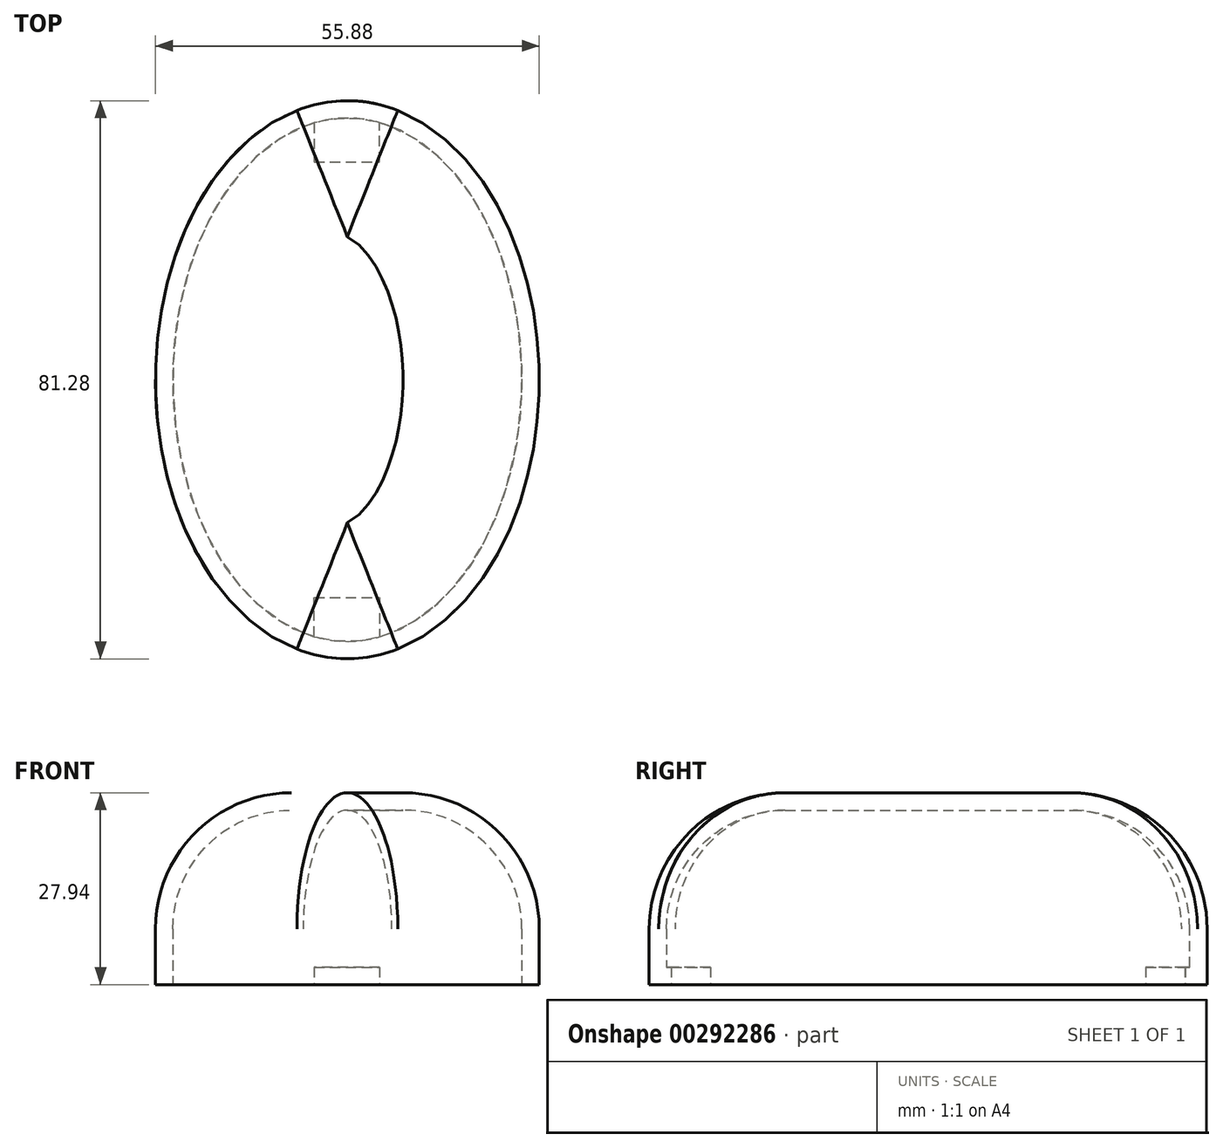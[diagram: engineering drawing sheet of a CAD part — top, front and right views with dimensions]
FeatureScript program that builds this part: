
annotation { "Feature Type Name" : "Feature", "Feature Type Description" : "" }
export const myFeature = defineFeature(function(context is Context, id is Id, definition is map)
    precondition{}
    {
        {
            var Q0;
            Q0=qCreatedBy(makeId("Top.planeOp"),FACE);
            var sketch = newSketch(context, id + "F0", { "sketchPlane" : qUnion([Q0])});
            skEllipse(sketch, "E0", {"center": v(0, 0) * mm, "majorRadius": 38.1 * mm, "minorRadius": 25.4 * mm, "majorAxis": v(0, 1)});
            skSolve(sketch);
        }
        {
            var Q0;
            Q0=makeQuery(id+"F0.imprint","IMPRINT",FACE,{"disambiguationData":[TD([[makeQuery(id+"F0.imprint","IMPRINT",EDGE,{"derivedFrom":sQuery(id+"F0.wireOp",EDGE,"E0")}),1.0]])]});
            extrude(context, id + "F1", {"entities" : qUnion([Q0]), "depth" : 25.4 * mm});
        }
        {
            var Q0;
            Q0=makeQuery(id+"F1.opExtrude","CAP_EDGE",EDGE,{"disambiguationData":[OSD([sQuery(id+"F0.wireOp",EDGE,"E0")])],"isStart":false});
            fillet(context, id + "F2", {"entities" : qUnion([Q0]), "radius" : 17.27 * mm, "tangentPropagation" : true, "allowEdgeOverflow" : false});
        }
        {
            var Q0;
            Q0=makeQuery(id+"F1.opExtrude","CAP_FACE",FACE,{"disambiguationData":[OSD([sQuery(id+"F0.wireOp",EDGE,"E0")])],"isStart":true});
            shell(context, id + "F3", {"entities" : qUnion([Q0]), "thickness" : 2.54 * mm, "oppositeDirection" : true});
        }
        {
            var Q0;
            Q0=makeQuery(id+"F1.opExtrude","CAP_FACE",FACE,{"disambiguationData":[OSD([sQuery(id+"F0.wireOp",EDGE,"E0")])],"isStart":true});
            var sketch = newSketch(context, id + "F4", { "sketchPlane" : qUnion([Q0])});
            skSolve(sketch);
        }
        {
            var Q0;
            {var subQ0=sQuery(id+"F0.wireOp",EDGE,"E0");var subQ1=makeQuery(id+"F1.opExtrude","CAP_EDGE",EDGE,{"disambiguationData":[OSD([subQ0])],"isStart":true});Q0=makeQuery(id+"F4.imprint","IMPRINT",FACE,{"disambiguationData":[TD([[makeQuery(id+"F4.imprint","IMPRINT",EDGE,{"derivedFrom":subQ1}),-1.0]])]});}
            var sketch = newSketch(context, id + "F5", { "sketchPlane" : qUnion([Q0])});
            skLineSegment(sketch, "E1", {"start": v(-4.83, 37.4) * mm, "end": v(-4.83, 31.7) * mm});
            skLineSegment(sketch, "E2", {"start": v(-4.83, 31.7) * mm, "end": v(4.7, 31.7) * mm});
            skLineSegment(sketch, "E3", {"start": v(4.7, 31.7) * mm, "end": v(4.7, 37.44) * mm});
            skArc(sketch, "E4", {"start": v(4.7, 37.44) * mm, "mid": v(-0.07, 38.14) * mm, "end": v(-4.83, 37.4) * mm});
            skLineSegment(sketch, "E5.MirrorCS", {"start": v(-4.83, -31.7) * mm, "end": v(4.7, -31.7) * mm});
            skLineSegment(sketch, "E6.MirrorCS", {"start": v(-4.83, -37.4) * mm, "end": v(-4.83, -31.7) * mm});
            skArc(sketch, "E7.MirrorCS", {"start": v(4.7, -37.44) * mm, "mid": v(-0.07, -38.14) * mm, "end": v(-4.83, -37.4) * mm});
            skLineSegment(sketch, "E8.MirrorCS", {"start": v(4.7, -31.7) * mm, "end": v(4.7, -37.44) * mm});
            skSolve(sketch);
        }
        {
            var Q0;
            {var subQ0=sQuery(id+"F5.wireOp",EDGE,"E1");Q0=makeQuery(id+"F5.imprint","IMPRINT",FACE,{"disambiguationData":[TD([[makeQuery(id+"F5.imprint","IMPRINT",EDGE,{"derivedFrom":subQ0}),1.0]])]});}
            var Q1;
            Q1=makeQuery(id+"F5.imprint","IMPRINT",FACE,{"disambiguationData":[TD([[makeQuery(id+"F5.imprint","IMPRINT",EDGE,{"derivedFrom":sQuery(id+"F5.wireOp",EDGE,"E5.MirrorCS")}),-1.0]])]});
            extrude(context, id + "F6", {"entities" : qUnion([Q0, Q1]), "operationType" : NewBodyOperationType.ADD, "oppositeDirection" : true, "depth" : 2.54 * mm});
        }
    });
